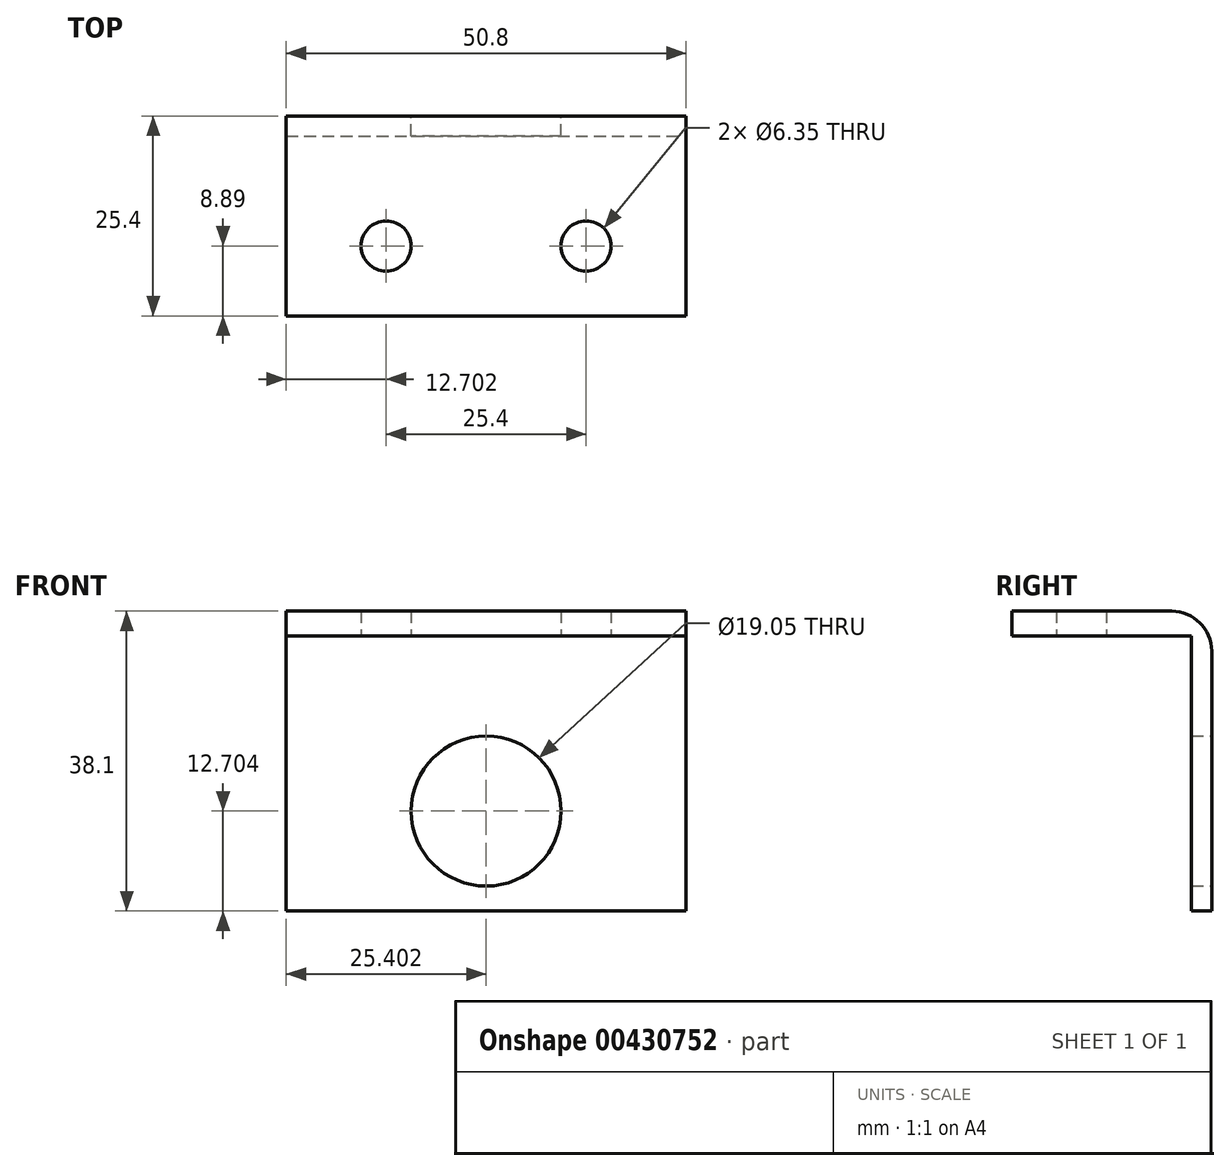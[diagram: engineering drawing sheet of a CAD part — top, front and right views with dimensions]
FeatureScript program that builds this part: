
annotation { "Feature Type Name" : "Feature", "Feature Type Description" : "" }
export const myFeature = defineFeature(function(context is Context, id is Id, definition is map)
    precondition{}
    {
        {
            var Q0;
            Q0=qCreatedBy(makeId("Front.planeOp"),FACE);
            var sketch = newSketch(context, id + "F0", { "sketchPlane" : qUnion([Q0])});
            skLineSegment(sketch, "E0.bottom", {"start": v(-32.89, 1.52) * mm, "end": v(17.91, 1.52) * mm});
            skLineSegment(sketch, "E0.top", {"start": v(-32.89, -36.58) * mm, "end": v(17.91, -36.58) * mm});
            skLineSegment(sketch, "E0.left", {"start": v(-32.89, 1.52) * mm, "end": v(-32.89, -36.58) * mm});
            skLineSegment(sketch, "E0.right", {"start": v(17.91, 1.52) * mm, "end": v(17.91, -36.58) * mm});
            skCircle(sketch, "E1", {"center": v(-7.49, -23.88) * mm, "radius": 9.53 * mm});
            skLineSegment(sketch, "E2", {"start": v(17.91, -1.64) * mm, "end": v(-32.89, -1.64) * mm});
            skSolve(sketch);
        }
        {
            var Q0;
            {var subQ0=sQuery(id+"F0.wireOp",EDGE,"E0.top");Q0=makeQuery(id+"F0.imprint","IMPRINT",FACE,{"disambiguationData":[TD([[makeQuery(id+"F0.imprint","IMPRINT",EDGE,{"derivedFrom":subQ0}),1.0]])]});}
            extrude(context, id + "F1", {"entities" : qUnion([Q0]), "depth" : 2.54 * mm, "offsetDistance" : 25.4 * mm});
        }
        {
            var Q0;
            {var subQ0=sQuery(id+"F0.wireOp",EDGE,"E0.bottom");Q0=makeQuery(id+"F0.imprint","IMPRINT",FACE,{"disambiguationData":[TD([[makeQuery(id+"F0.imprint","IMPRINT",EDGE,{"derivedFrom":subQ0}),-1.0]])]});}
            extrude(context, id + "F2", {"entities" : qUnion([Q0]), "operationType" : NewBodyOperationType.ADD, "depth" : 25.4 * mm, "offsetDistance" : 25.4 * mm});
        }
        {
            var Q0;
            Q0=makeQuery(id+"F1.opExtrude","CAP_EDGE",EDGE,{"disambiguationData":[OSD([sQuery(id+"F0.wireOp",EDGE,"E2")])],"isStart":false});
            var Q1;
            Q1=makeQuery(id+"F2.opExtrude","CAP_EDGE",EDGE,{"disambiguationData":[OSD([sQuery(id+"F0.wireOp",EDGE,"E0.bottom")])],"isStart":true});
            fillet(context, id + "F3", {"entities" : qUnion([Q0, Q1]), "radius" : 5.08 * mm, "tangentPropagation" : true, "allowEdgeOverflow" : false});
        }
        {
            var Q0;
            Q0=makeQuery(id+"F2.opExtrude","SWEPT_FACE",FACE,{"disambiguationData":[OSD([sQuery(id+"F0.wireOp",EDGE,"E2")])]});
            var sketch = newSketch(context, id + "F4", { "sketchPlane" : qUnion([Q0])});
            skCircle(sketch, "E3", {"center": v(-20.19, 16.51) * mm, "radius": 3.18 * mm});
            skCircle(sketch, "E4", {"center": v(5.21, 16.51) * mm, "radius": 3.18 * mm});
            skLineSegment(sketch, "E5", {"start": v(-20.19, 16.51) * mm, "end": v(5.21, 16.51) * mm, "construction": true});
            skLineSegment(sketch, "E6", {"start": v(-7.49, 7.62) * mm, "end": v(-7.49, 25.4) * mm, "construction": true});
            skPoint(sketch, "E7", {"position": v(-7.49, 16.51) * mm});
            skSolve(sketch);
        }
        {
            var Q0;
            Q0 = qSketchRegion(id + "F4", true);
            extrude(context, id + "F5", {"entities" : qUnion([Q0]), "operationType" : NewBodyOperationType.REMOVE, "oppositeDirection" : true, "depth" : 25.4 * mm, "offsetDistance" : 25.4 * mm});
        }
    });
